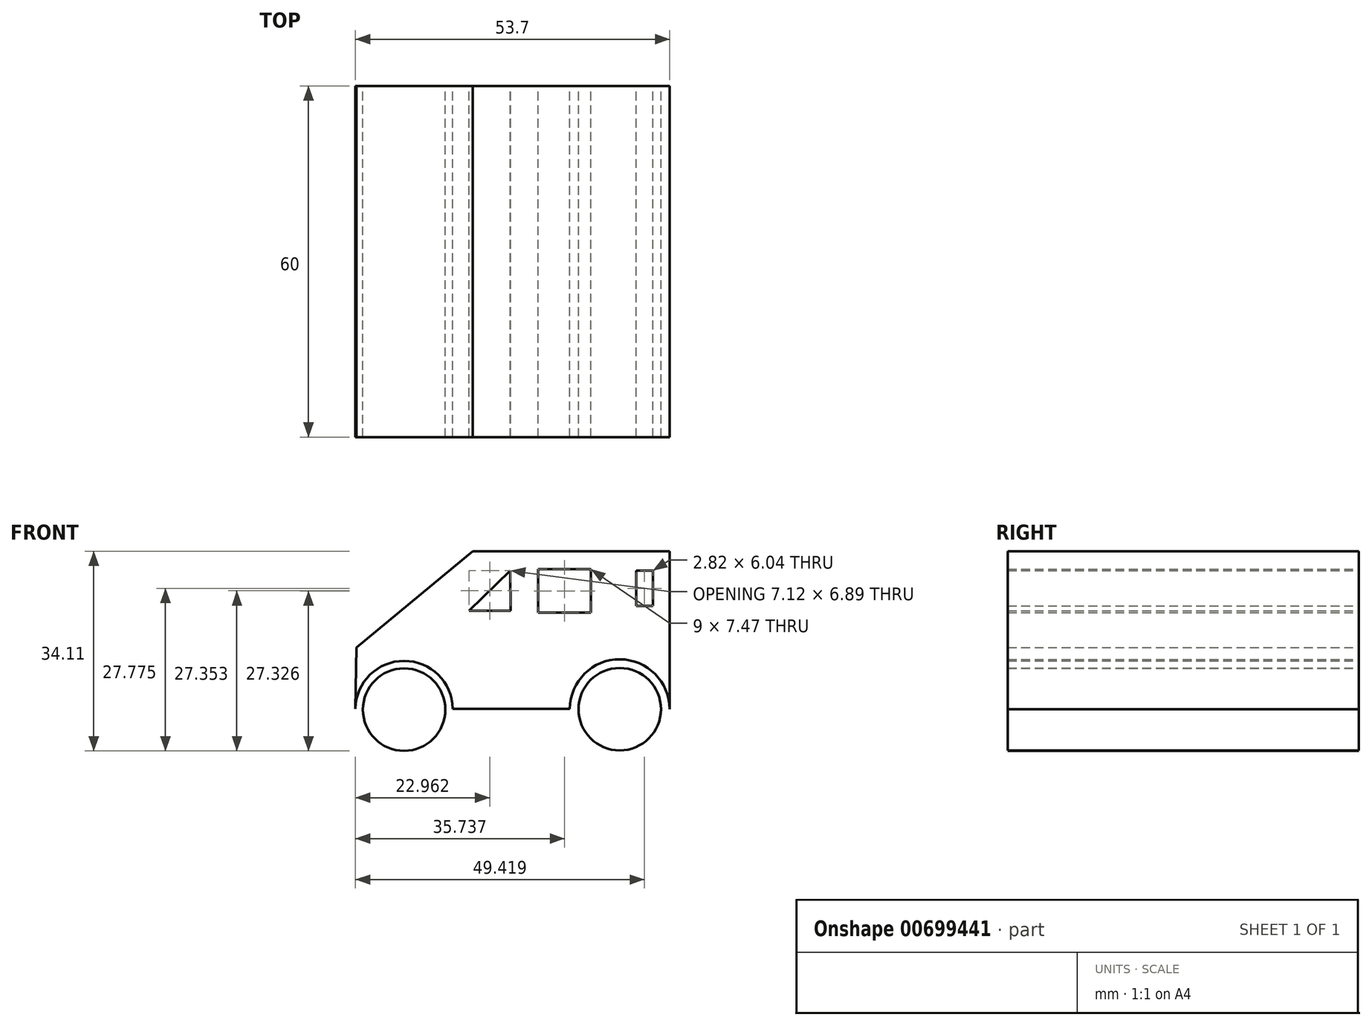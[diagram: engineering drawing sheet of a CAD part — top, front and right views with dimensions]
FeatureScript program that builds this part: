
annotation { "Feature Type Name" : "Feature", "Feature Type Description" : "" }
export const myFeature = defineFeature(function(context is Context, id is Id, definition is map)
    precondition{}
    {
        {
            var Q0;
            Q0=qCreatedBy(makeId("Front.planeOp"),FACE);
            var sketch = newSketch(context, id + "F0", { "sketchPlane" : qUnion([Q0])});
            skLineSegment(sketch, "E0", {"start": v(-49.34, 0) * mm, "end": v(-29.34, 0) * mm});
            skLineSegment(sketch, "E1", {"start": v(-49.34, 0) * mm, "end": v(-49.34, 10.42) * mm});
            skLineSegment(sketch, "E2", {"start": v(-29.34, 0) * mm, "end": v(-29.34, 10.65) * mm});
            skLineSegment(sketch, "E3", {"start": v(-49.34, 10.42) * mm, "end": v(-65.8, 10.42) * mm});
            skLineSegment(sketch, "E4", {"start": v(-65.8, 10.42) * mm, "end": v(-45.94, 26.9) * mm});
            skLineSegment(sketch, "E5", {"start": v(-45.94, 26.9) * mm, "end": v(-40.63, 26.9) * mm});
            skLineSegment(sketch, "E6", {"start": v(-40.63, 26.9) * mm, "end": v(-57.57, 10.42) * mm});
            skLineSegment(sketch, "E7", {"start": v(-37, 26.9) * mm, "end": v(-37, 0) * mm});
            skLineSegment(sketch, "E8", {"start": v(-39.51, 23.6) * mm, "end": v(-46.59, 16.7) * mm});
            skLineSegment(sketch, "E9", {"start": v(-46.59, 16.7) * mm, "end": v(-39.47, 16.7) * mm});
            skLineSegment(sketch, "E10", {"start": v(-39.47, 16.7) * mm, "end": v(-39.51, 23.6) * mm});
            skLineSegment(sketch, "E11", {"start": v(-12.3, 26.9) * mm, "end": v(-12.3, -0.1) * mm});
            skLineSegment(sketch, "E12", {"start": v(-29.34, 10.65) * mm, "end": v(-12.3, 10.65) * mm});
            skLineSegment(sketch, "E13", {"start": v(-25.79, 10.65) * mm, "end": v(-20.82, 19.71) * mm});
            skPoint(sketch, "E13.endSnap0", {"position": v(-20.82, 10.65) * mm});
            skLineSegment(sketch, "E14", {"start": v(-20.82, 19.71) * mm, "end": v(-20.82, 26.9) * mm});
            skLineSegment(sketch, "E15", {"start": v(-34.75, 23.86) * mm, "end": v(-34.75, 16.4) * mm});
            skLineSegment(sketch, "E16", {"start": v(-34.75, 16.4) * mm, "end": v(-25.75, 16.4) * mm});
            skLineSegment(sketch, "E17", {"start": v(-25.75, 16.4) * mm, "end": v(-25.75, 23.86) * mm});
            skLineSegment(sketch, "E18", {"start": v(-25.75, 23.86) * mm, "end": v(-34.75, 23.86) * mm});
            skLineSegment(sketch, "E19", {"start": v(-17.98, 23.6) * mm, "end": v(-17.98, 17.55) * mm});
            skLineSegment(sketch, "E20", {"start": v(-17.98, 17.55) * mm, "end": v(-15.16, 17.55) * mm});
            skLineSegment(sketch, "E21", {"start": v(-15.16, 17.55) * mm, "end": v(-15.16, 23.6) * mm});
            skLineSegment(sketch, "E22", {"start": v(-15.16, 23.6) * mm, "end": v(-17.98, 23.6) * mm});
            skLineSegment(sketch, "E23", {"start": v(-12.3, 26.9) * mm, "end": v(-40.63, 26.9) * mm});
            skLineSegment(sketch, "E24", {"start": v(-65.8, 10.42) * mm, "end": v(-66, 0) * mm});
            skArc(sketch, "E25", {"start": v(-49.34, 0) * mm, "mid": v(-57.67, 8.17) * mm, "end": v(-66, 0) * mm});
            skArc(sketch, "E26", {"start": v(-12.3, -0.1) * mm, "mid": v(-20.77, 8.43) * mm, "end": v(-29.34, 0) * mm});
            skCircle(sketch, "E27", {"center": v(-57.67, -0.16) * mm, "radius": 7.04 * mm});
            skCircle(sketch, "E28", {"center": v(-20.82, -0.1) * mm, "radius": 7.04 * mm});
            skSolve(sketch);
        }
        {
            var Q0;
            Q0 = qSketchRegion(id + "F0", true);
            extrude(context, id + "F1", {"entities" : qUnion([Q0]), "depth" : 60 * mm, "offsetDistance" : 25 * mm});
        }
    });
